# Revit family: Overhead_Door-CHIOHD-MaxDock_Direct_Drive
name_source: partatom
category: Specialty Equipment
units: mm (PartAtom-declared; Revit-internal decimal feet)

## family parameters
Always vertical = Yes
Classification Number = 23.30.10.21
Cut with Voids When Loaded = No
Enable Cutting in Views = No
Host = Wall
Maintain Annotation Orientation = No
Part Type = Normal
Room Calculation Point = No
Round Connector Dimension = Use Diameter
Shared = No

## types (1)
- MaxDock DD - 350 - Gray - 1/4" Reinforced Rubber Curtain
    Apparent Load Phase 1 = 0 VA
    Apparent Load Phase 2 = 0 VA
    Apparent Load Phase 3 = 0 VA
    Assembly Code = B2030410
    Axis Offset = 0' - 11"
    Closing Speed = 12 inches / second
    Curtain Material = Rubber - C.H.I Overhead Doors - Reinforced Black Rubber
    Default Elevation = 0' - 0"
    Description = Hight Performance Rubber Door
    Door Rail Depth = 0' - 4 3/4"
    Door Rail Width = 0' - 4"
    Keynote = 08 30 00
    Load Classification = Motor
    Manufacturer = C.H.I. Overhead Doors
    Manufacturer Fax Number = 800-677-2650
    Model = 350
    Motor Anchorage = 0' - 7"
    Motor Distance from Wall = 2' - 2 7/8"
    Number of Poles = 3
    Opening Speed = 12 inches / second
    Panel Thickness = 0' - 0 1/4"
    Power Factor = 1
    Product Documentation Link = https://www.chiohd.com
    Product Page URL = https://www.chiohd.com
    Shutter Box Depth = 1' - 3"
    Shutter Box Height = 1' - 3"
    Steel Gauge = 1/4"
    URL = https://www.chiohd.com
    Version = 2021-v1.a
    Voltage = 460 V
    Warranty URL = https://www.chiohd.com

## geometry (parser evidence)
native form markers: Extrusion x1, Sweep x7
no freeform markers — native parametric forms only
